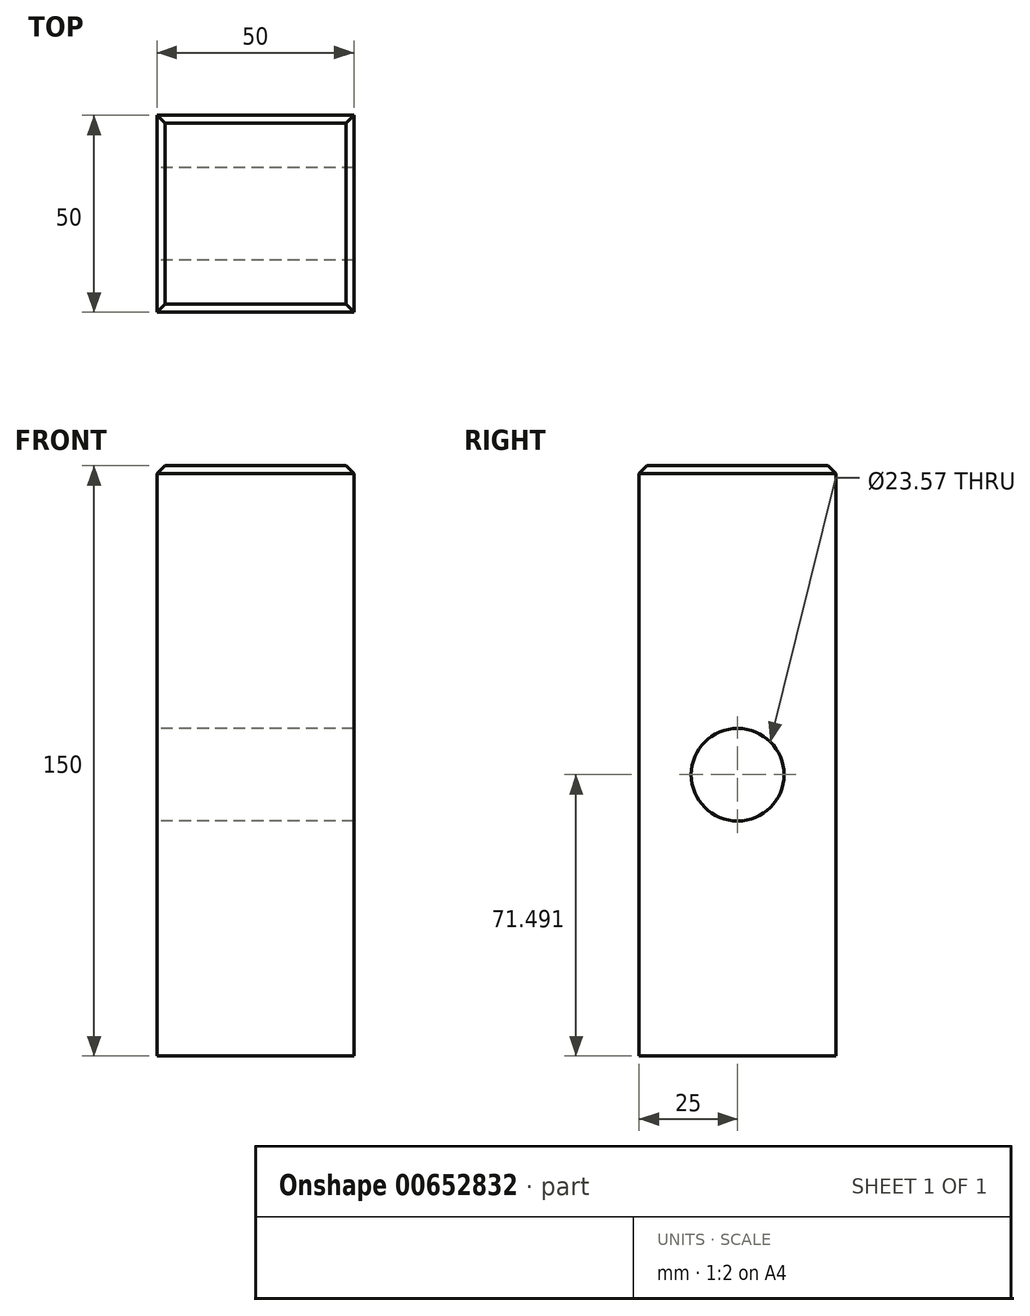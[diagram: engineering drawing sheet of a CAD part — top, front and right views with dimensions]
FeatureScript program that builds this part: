
annotation { "Feature Type Name" : "Feature", "Feature Type Description" : "" }
export const myFeature = defineFeature(function(context is Context, id is Id, definition is map)
    precondition{}
    {
        {
            var Q0;
            Q0=qCreatedBy(makeId("Top.planeOp"),FACE);
            var sketch = newSketch(context, id + "F0", { "sketchPlane" : qUnion([Q0])});
            skLineSegment(sketch, "E0", {"start": v(-50, 0) * mm, "end": v(-50, -50) * mm});
            skLineSegment(sketch, "E1", {"start": v(-50, -50) * mm, "end": v(0, -50) * mm});
            skLineSegment(sketch, "E2", {"start": v(0, -50) * mm, "end": v(0, 0) * mm});
            skLineSegment(sketch, "E3", {"start": v(0, 0) * mm, "end": v(-50, 0) * mm});
            skSolve(sketch);
        }
        {
            var Q0;
            Q0=makeQuery(id+"F0.imprint","IMPRINT",FACE,{"disambiguationData":[TD([[makeQuery(id+"F0.imprint","IMPRINT",EDGE,{"derivedFrom":sQuery(id+"F0.wireOp",EDGE,"E0")}),1.0]])]});
            extrude(context, id + "F1", {"entities" : qUnion([Q0]), "depth" : 150 * mm, "offsetDistance" : 25 * mm});
        }
        {
            var Q0;
            Q0=makeQuery(id+"F1.opExtrude","SWEPT_FACE",FACE,{"disambiguationData":[OSD([sQuery(id+"F0.wireOp",EDGE,"E0")])]});
            var sketch = newSketch(context, id + "F2", { "sketchPlane" : qUnion([Q0])});
            skCircle(sketch, "E4", {"center": v(25, 71.5) * mm, "radius": 11.78 * mm});
            skSolve(sketch);
        }
        {
            var Q0;
            Q0=makeQuery(id+"F2.imprint","IMPRINT",FACE,{"disambiguationData":[TD([[makeQuery(id+"F2.imprint","IMPRINT",EDGE,{"derivedFrom":sQuery(id+"F2.wireOp",EDGE,"E4")}),1.0]])]});
            extrude(context, id + "F3", {"entities" : qUnion([Q0]), "operationType" : NewBodyOperationType.REMOVE, "oppositeDirection" : true, "depth" : 131.63 * mm, "offsetDistance" : 25 * mm});
        }
        {
            var Q0;
            Q0=makeQuery(id+"F1.opExtrude","CAP_EDGE",EDGE,{"disambiguationData":[OSD([sQuery(id+"F0.wireOp",EDGE,"E0")])],"isStart":false});
            var Q1;
            Q1=makeQuery(id+"F1.opExtrude","CAP_EDGE",EDGE,{"disambiguationData":[OSD([sQuery(id+"F0.wireOp",EDGE,"E2")])],"isStart":false});
            var Q2;
            Q2=makeQuery(id+"F1.opExtrude","CAP_EDGE",EDGE,{"disambiguationData":[OSD([sQuery(id+"F0.wireOp",EDGE,"E1")])],"isStart":false});
            var Q3;
            Q3=makeQuery(id+"F1.opExtrude","CAP_EDGE",EDGE,{"disambiguationData":[OSD([sQuery(id+"F0.wireOp",EDGE,"E3")])],"isStart":false});
            chamfer(context, id + "F4", {"entities" : qUnion([Q0, Q1, Q2, Q3]), "width" : 2 * mm, "tangentPropagation" : true});
        }
    });
